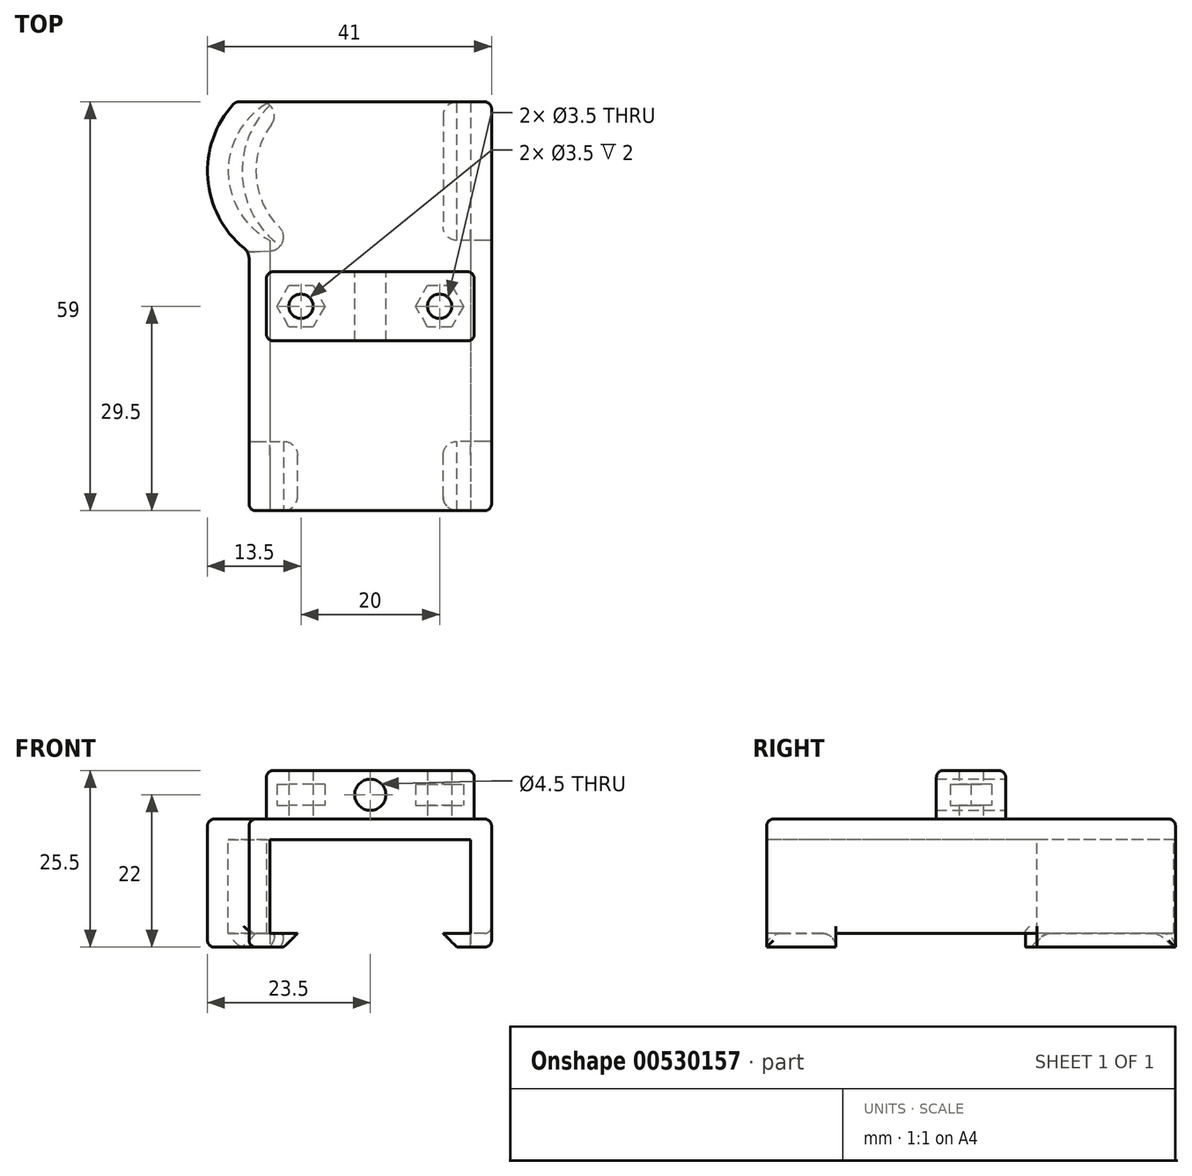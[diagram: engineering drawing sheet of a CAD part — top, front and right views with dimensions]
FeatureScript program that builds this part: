
annotation { "Feature Type Name" : "Feature", "Feature Type Description" : "" }
export const myFeature = defineFeature(function(context is Context, id is Id, definition is map)
    precondition{}
    {
        {
            var Q0;
            Q0=qCreatedBy(makeId("Top.planeOp"),FACE);
            var sketch = newSketch(context, id + "F0", { "sketchPlane" : qUnion([Q0])});
            skLineSegment(sketch, "E0.bottom", {"start": v(-14.5, 29.5) * mm, "end": v(14.5, 29.5) * mm});
            skLineSegment(sketch, "E0.top", {"start": v(-14.5, -29.5) * mm, "end": v(14.5, -29.5) * mm});
            skLineSegment(sketch, "E0.left", {"start": v(-14.5, 9.5) * mm, "end": v(-14.5, -29.5) * mm});
            skLineSegment(sketch, "E0.right", {"start": v(14.5, 29.5) * mm, "end": v(14.5, -29.5) * mm});
            skPoint(sketch, "E0.middle", {"position": v(0, 0) * mm});
            skArc(sketch, "E1", {"start": v(-14.5, 29.5) * mm, "mid": v(-20.5, 19.5) * mm, "end": v(-14.5, 9.5) * mm});
            skLineSegment(sketch, "E2", {"start": v(-29.83, 19.5) * mm, "end": v(45.18, 19.5) * mm, "construction": true});
            skPoint(sketch, "E3", {"position": v(-14.5, 29.5) * mm});
            skPoint(sketch, "E4", {"position": v(-14.5, 9.5) * mm});
            skSolve(sketch);
        }
        {
            var Q0;
            Q0=makeQuery(id+"F0.imprint","IMPRINT",FACE,{"disambiguationData":[TD([[makeQuery(id+"F0.imprint","IMPRINT",EDGE,{"derivedFrom":sQuery(id+"F0.wireOp",EDGE,"E0.bottom")}),-1.0]])]});
            extrude(context, id + "F1", {"entities" : qUnion([Q0]), "oppositeDirection" : true, "depth" : 3 * mm, "offsetDistance" : 25 * mm});
        }
        {
            var Q0;
            Q0=makeQuery(id+"F1.opExtrude","CAP_FACE",FACE,{"disambiguationData":[OSD([sQuery(id+"F0.wireOp",EDGE,"E0.bottom"),sQuery(id+"F0.wireOp",EDGE,"E0.top"),sQuery(id+"F0.wireOp",EDGE,"E0.left"),sQuery(id+"F0.wireOp",EDGE,"E0.right"),sQuery(id+"F0.wireOp",EDGE,"E1")])],"isStart":false});
            var sketch = newSketch(context, id + "F2", { "sketchPlane" : qUnion([Q0])});
            skLineSegment(sketch, "E5.0", {"start": v(14.5, -29.5) * mm, "end": v(14.5, 29.5) * mm});
            skLineSegment(sketch, "E6.0", {"start": v(-14.5, -9.5) * mm, "end": v(-14.5, 29.5) * mm});
            skArc(sketch, "E7.0", {"start": v(-14.5, -29.5) * mm, "mid": v(-20.5, -19.5) * mm, "end": v(-14.5, -9.5) * mm});
            skLineSegment(sketch, "E8.0", {"start": v(17.5, -29.5) * mm, "end": v(17.5, 29.5) * mm});
            skLineSegment(sketch, "E9.0", {"start": v(-17.5, -7.84) * mm, "end": v(-17.5, 29.5) * mm});
            skArc(sketch, "E9.1", {"start": v(-15.91, -32.15) * mm, "mid": v(-23.47, -20.43) * mm, "end": v(-17.5, -7.84) * mm});
            skLineSegment(sketch, "E10", {"start": v(14.5, -29.5) * mm, "end": v(17.5, -29.5) * mm});
            skLineSegment(sketch, "E11", {"start": v(14.5, 29.5) * mm, "end": v(17.5, 29.5) * mm});
            skLineSegment(sketch, "E12", {"start": v(-14.5, 29.5) * mm, "end": v(-17.5, 29.5) * mm});
            skLineSegment(sketch, "E13", {"start": v(-14.5, -29.5) * mm, "end": v(-19.44, -29.5) * mm});
            skSolve(sketch);
        }
        {
            var Q0;
            Q0=makeQuery(id+"F2.imprint","IMPRINT",FACE,{"disambiguationData":[TD([[makeQuery(id+"F2.imprint","IMPRINT",EDGE,{"derivedFrom":sQuery(id+"F2.wireOp",EDGE,"E5.0")}),-1.0]])]});
            var Q1;
            Q1=makeQuery(id+"F2.imprint","IMPRINT",FACE,{"disambiguationData":[TD([[makeQuery(id+"F2.imprint","IMPRINT",EDGE,{"derivedFrom":sQuery(id+"F2.wireOp",EDGE,"E6.0")}),1.0]])]});
            var Q2;
            Q2=makeQuery(id+"F1.opExtrude","CAP_FACE",FACE,{"disambiguationData":[OSD([sQuery(id+"F0.wireOp",EDGE,"E0.bottom"),sQuery(id+"F0.wireOp",EDGE,"E0.top"),sQuery(id+"F0.wireOp",EDGE,"E0.left"),sQuery(id+"F0.wireOp",EDGE,"E0.right"),sQuery(id+"F0.wireOp",EDGE,"E1")])],"isStart":true});
            extrude(context, id + "F3", {"entities" : qUnion([Q0, Q1]), "operationType" : NewBodyOperationType.ADD, "depth" : 13.5 * mm, "offsetDistance" : 25 * mm, "hasSecondDirection" : true, "secondDirectionBound" : BoundingType.UP_TO_SURFACE, "secondDirectionOppositeDirection" : true, "secondDirectionDepth" : 25 * mm, "secondDirectionBoundEntityFace" : qUnion([Q2])});
        }
        {
            var Q0;
            Q0=makeQuery(id+"F3.opExtrude","CAP_FACE",FACE,{"disambiguationData":[OSD([sQuery(id+"F2.wireOp",EDGE,"E6.0"),sQuery(id+"F2.wireOp",EDGE,"E7.0"),sQuery(id+"F2.wireOp",EDGE,"E9.0"),sQuery(id+"F2.wireOp",EDGE,"E9.1"),sQuery(id+"F2.wireOp",EDGE,"E12"),sQuery(id+"F2.wireOp",EDGE,"E13")])],"isStart":false});
            var sketch = newSketch(context, id + "F4", { "sketchPlane" : qUnion([Q0])});
            skLineSegment(sketch, "E14.bottom", {"start": v(-17.5, 29.5) * mm, "end": v(-10.5, 29.5) * mm});
            skLineSegment(sketch, "E14.top", {"start": v(-17.5, 19.5) * mm, "end": v(-10.5, 19.5) * mm});
            skLineSegment(sketch, "E14.left", {"start": v(-17.5, 29.5) * mm, "end": v(-17.5, 19.5) * mm});
            skLineSegment(sketch, "E14.right", {"start": v(-10.5, 29.5) * mm, "end": v(-10.5, 19.5) * mm});
            skLineSegment(sketch, "E15.bottom", {"start": v(17.5, 29.5) * mm, "end": v(10.5, 29.5) * mm});
            skLineSegment(sketch, "E15.top", {"start": v(17.5, 19.5) * mm, "end": v(10.5, 19.5) * mm});
            skLineSegment(sketch, "E15.left", {"start": v(17.5, 29.5) * mm, "end": v(17.5, 19.5) * mm});
            skLineSegment(sketch, "E15.right", {"start": v(10.5, 29.5) * mm, "end": v(10.5, 19.5) * mm});
            skLineSegment(sketch, "E16.bottom", {"start": v(17.5, -29.5) * mm, "end": v(10.5, -29.5) * mm});
            skLineSegment(sketch, "E16.top", {"start": v(17.5, -9.5) * mm, "end": v(10.5, -9.5) * mm});
            skLineSegment(sketch, "E16.left", {"start": v(17.5, -29.5) * mm, "end": v(17.5, -9.5) * mm});
            skLineSegment(sketch, "E16.right", {"start": v(10.5, -29.5) * mm, "end": v(10.5, -9.5) * mm});
            skArc(sketch, "E17.0", {"start": v(-19.44, -29.5) * mm, "mid": v(-23.44, -18.22) * mm, "end": v(-17.5, -7.84) * mm});
            skArc(sketch, "E18", {"start": v(-7.27, -8.36) * mm, "mid": v(-16.37, -17.8) * mm, "end": v(-10.5, -29.5) * mm});
            skLineSegment(sketch, "E19", {"start": v(-19.44, -29.5) * mm, "end": v(-10.5, -29.5) * mm});
            skLineSegment(sketch, "E20", {"start": v(-17.5, -7.84) * mm, "end": v(-7.27, -8.36) * mm});
            skSolve(sketch);
        }
        {
            var Q0;
            Q0 = qSketchRegion(id + "F4", true);
            extrude(context, id + "F5", {"entities" : qUnion([Q0]), "operationType" : NewBodyOperationType.ADD, "depth" : 2 * mm, "offsetDistance" : 25 * mm});
        }
        {
            var Q0;
            Q0=makeQuery(id+"F5.opExtrude","SWEPT_EDGE",EDGE,{"disambiguationData":[OSD([sQuery(id+"F4.wireOp",EDGE,"E18"),sQuery(id+"F4.wireOp",EDGE,"E20")])]});
            var Q1;
            Q1=makeQuery(id+"F5.opExtrude","SWEPT_EDGE",EDGE,{"disambiguationData":[OSD([sQuery(id+"F4.wireOp",EDGE,"E18"),sQuery(id+"F4.wireOp",EDGE,"E19")])]});
            var Q2;
            Q2=makeQuery(id+"F5.opExtrude","SWEPT_EDGE",EDGE,{"disambiguationData":[OSD([sQuery(id+"F4.wireOp",EDGE,"E16.top"),sQuery(id+"F4.wireOp",EDGE,"E16.right")])]});
            var Q3;
            Q3=makeQuery(id+"F5.opExtrude","SWEPT_EDGE",EDGE,{"disambiguationData":[OSD([sQuery(id+"F4.wireOp",EDGE,"E16.bottom"),sQuery(id+"F4.wireOp",EDGE,"E16.right")])]});
            var Q4;
            Q4=makeQuery(id+"F5.opExtrude","SWEPT_EDGE",EDGE,{"disambiguationData":[OSD([sQuery(id+"F4.wireOp",EDGE,"E15.bottom"),sQuery(id+"F4.wireOp",EDGE,"E15.right")])]});
            var Q5;
            Q5=makeQuery(id+"F5.opExtrude","SWEPT_EDGE",EDGE,{"disambiguationData":[OSD([sQuery(id+"F4.wireOp",EDGE,"E15.top"),sQuery(id+"F4.wireOp",EDGE,"E15.right")])]});
            var Q6;
            Q6=makeQuery(id+"F5.opExtrude","SWEPT_EDGE",EDGE,{"disambiguationData":[OSD([sQuery(id+"F4.wireOp",EDGE,"E14.top"),sQuery(id+"F4.wireOp",EDGE,"E14.right")])]});
            var Q7;
            Q7=makeQuery(id+"F5.opExtrude","SWEPT_EDGE",EDGE,{"disambiguationData":[OSD([sQuery(id+"F4.wireOp",EDGE,"E14.bottom"),sQuery(id+"F4.wireOp",EDGE,"E14.right")])]});
            var Q8;
            Q8=makeQuery(id+"F3.opExtrude","SWEPT_EDGE",EDGE,{"disambiguationData":[OSD([sQuery(id+"F2.wireOp",EDGE,"E9.0"),sQuery(id+"F2.wireOp",EDGE,"E9.1")])]});
            var Q9;
            {var subQ0=sQuery(id+"F4.wireOp",EDGE,"E16.top");Q9=makeQuery(id+"F5.boolean.opBoolean","SPLIT",EDGE,{"disambiguationData":[topologyDisambiguationEdgeConnected([makeQuery(id+"F3.opExtrude","CAP_FACE",FACE,{"disambiguationData":[OSD([sQuery(id+"F2.wireOp",EDGE,"E5.0"),sQuery(id+"F2.wireOp",EDGE,"E8.0"),sQuery(id+"F2.wireOp",EDGE,"E10"),sQuery(id+"F2.wireOp",EDGE,"E11")])],"isStart":false})])],"derivedFrom":makeQuery(id+"F5.opExtrude","CAP_EDGE",EDGE,{"disambiguationData":[OSD([subQ0])],"isStart":true})});}
            var Q10;
            {var subQ0=sQuery(id+"F4.wireOp",EDGE,"E14.top");Q10=makeQuery(id+"F5.boolean.opBoolean","SPLIT",EDGE,{"disambiguationData":[topologyDisambiguationEdgeConnected([makeQuery(id+"F3.opExtrude","CAP_FACE",FACE,{"disambiguationData":[OSD([sQuery(id+"F2.wireOp",EDGE,"E6.0"),sQuery(id+"F2.wireOp",EDGE,"E7.0"),sQuery(id+"F2.wireOp",EDGE,"E9.0"),sQuery(id+"F2.wireOp",EDGE,"E9.1"),sQuery(id+"F2.wireOp",EDGE,"E12"),sQuery(id+"F2.wireOp",EDGE,"E13")])],"isStart":false})])],"derivedFrom":makeQuery(id+"F5.opExtrude","CAP_EDGE",EDGE,{"disambiguationData":[OSD([subQ0])],"isStart":true})});}
            var Q11;
            {var subQ0=sQuery(id+"F4.wireOp",EDGE,"E15.top");Q11=makeQuery(id+"F5.boolean.opBoolean","SPLIT",EDGE,{"disambiguationData":[topologyDisambiguationEdgeConnected([makeQuery(id+"F3.opExtrude","CAP_FACE",FACE,{"disambiguationData":[OSD([sQuery(id+"F2.wireOp",EDGE,"E5.0"),sQuery(id+"F2.wireOp",EDGE,"E8.0"),sQuery(id+"F2.wireOp",EDGE,"E10"),sQuery(id+"F2.wireOp",EDGE,"E11")])],"isStart":false})])],"derivedFrom":makeQuery(id+"F5.opExtrude","CAP_EDGE",EDGE,{"disambiguationData":[OSD([subQ0])],"isStart":true})});}
            fillet(context, id + "F6", {"entities" : qUnion([Q0, Q1, Q2, Q3, Q4, Q5, Q6, Q7, Q8, Q9, Q10, Q11]), "tangentPropagation" : true, "radius" : 2 * mm, "defaultsChanged" : false, "vertexSettings" : [], "allowEdgeOverflow" : false});
        }
        {
            var Q0;
            Q0=makeQuery(id+"F5.opExtrude","CAP_EDGE",EDGE,{"disambiguationData":[OSD([sQuery(id+"F4.wireOp",EDGE,"E17.0")])],"isStart":false});
            var Q1;
            Q1=makeQuery(id+"F3.opExtrude","CAP_EDGE",EDGE,{"disambiguationData":[OSD([sQuery(id+"F2.wireOp",EDGE,"E9.0")])],"isStart":false});
            var Q2;
            Q2=makeQuery(id+"F5.opExtrude","CAP_EDGE",EDGE,{"disambiguationData":[OSD([sQuery(id+"F4.wireOp",EDGE,"E14.left")])],"isStart":false});
            var Q3;
            Q3=makeQuery(id+"F3.opExtrude","CAP_EDGE",EDGE,{"disambiguationData":[OSD([sQuery(id+"F2.wireOp",EDGE,"E9.0")])],"isStart":true});
            var Q4;
            Q4=makeQuery(id+"F3.opExtrude","CAP_EDGE",EDGE,{"disambiguationData":[OSD([sQuery(id+"F2.wireOp",EDGE,"E8.0")])],"isStart":false});
            var Q5;
            Q5=makeQuery(id+"F3.opExtrude","CAP_EDGE",EDGE,{"disambiguationData":[OSD([sQuery(id+"F2.wireOp",EDGE,"E8.0")])],"isStart":true});
            var Q6;
            Q6=makeQuery(id+"F3.boolean.opBoolean","MERGE",EDGE,{"derivedFrom":[makeQuery(id+"F1.opExtrude","CAP_EDGE",EDGE,{"disambiguationData":[OSD([sQuery(id+"F0.wireOp",EDGE,"E0.bottom")])],"isStart":true}),makeQuery(id+"F3.opExtrude","CAP_EDGE",EDGE,{"disambiguationData":[OSD([sQuery(id+"F2.wireOp",EDGE,"E10")])],"isStart":true}),makeQuery(id+"F3.opExtrude","CAP_EDGE",EDGE,{"disambiguationData":[OSD([sQuery(id+"F2.wireOp",EDGE,"E13")])],"isStart":true})]});
            var Q7;
            Q7=makeQuery(id+"F3.boolean.opBoolean","MERGE",EDGE,{"derivedFrom":[makeQuery(id+"F1.opExtrude","CAP_EDGE",EDGE,{"disambiguationData":[OSD([sQuery(id+"F0.wireOp",EDGE,"E0.top")])],"isStart":true}),makeQuery(id+"F3.opExtrude","CAP_EDGE",EDGE,{"disambiguationData":[OSD([sQuery(id+"F2.wireOp",EDGE,"E11")])],"isStart":true}),makeQuery(id+"F3.opExtrude","CAP_EDGE",EDGE,{"disambiguationData":[OSD([sQuery(id+"F2.wireOp",EDGE,"E12")])],"isStart":true})]});
            var Q8;
            Q8=makeQuery(id+"F5.boolean.opBoolean","MERGE",EDGE,{"derivedFrom":[makeQuery(id+"F3.opExtrude","SWEPT_EDGE",EDGE,{"disambiguationData":[OSD([sQuery(id+"F2.wireOp",EDGE,"E8.0"),sQuery(id+"F2.wireOp",EDGE,"E11")])]}),makeQuery(id+"F5.opExtrude","SWEPT_EDGE",EDGE,{"disambiguationData":[OSD([sQuery(id+"F4.wireOp",EDGE,"E15.bottom"),sQuery(id+"F4.wireOp",EDGE,"E15.left")])]})]});
            var Q9;
            Q9=makeQuery(id+"F5.boolean.opBoolean","MERGE",EDGE,{"derivedFrom":[makeQuery(id+"F3.opExtrude","SWEPT_EDGE",EDGE,{"disambiguationData":[OSD([sQuery(id+"F2.wireOp",EDGE,"E9.0"),sQuery(id+"F2.wireOp",EDGE,"E12")])]}),makeQuery(id+"F5.opExtrude","SWEPT_EDGE",EDGE,{"disambiguationData":[OSD([sQuery(id+"F4.wireOp",EDGE,"E14.bottom"),sQuery(id+"F4.wireOp",EDGE,"E14.left")])]})]});
            var Q10;
            Q10=makeQuery(id+"F5.boolean.opBoolean","MERGE",EDGE,{"derivedFrom":[makeQuery(id+"F3.opExtrude","SWEPT_EDGE",EDGE,{"disambiguationData":[OSD([sQuery(id+"F2.wireOp",EDGE,"E8.0"),sQuery(id+"F2.wireOp",EDGE,"E10")])]}),makeQuery(id+"F5.opExtrude","SWEPT_EDGE",EDGE,{"disambiguationData":[OSD([sQuery(id+"F4.wireOp",EDGE,"E16.bottom"),sQuery(id+"F4.wireOp",EDGE,"E16.left")])]})]});
            var Q11;
            Q11=makeQuery(id+"F5.boolean.opBoolean","MERGE",EDGE,{"derivedFrom":[makeQuery(id+"F3.opExtrude","SWEPT_EDGE",EDGE,{"disambiguationData":[OSD([sQuery(id+"F2.wireOp",EDGE,"E9.1"),sQuery(id+"F2.wireOp",EDGE,"E13")])]}),makeQuery(id+"F5.opExtrude","SWEPT_EDGE",EDGE,{"disambiguationData":[OSD([sQuery(id+"F4.wireOp",EDGE,"E17.0"),sQuery(id+"F4.wireOp",EDGE,"E19")])]})]});
            var Q12;
            Q12=makeQuery(id+"F5.opExtrude","CAP_EDGE",EDGE,{"disambiguationData":[OSD([sQuery(id+"F4.wireOp",EDGE,"E16.left")])],"isStart":false});
            var Q13;
            Q13=makeQuery(id+"F5.opExtrude","CAP_EDGE",EDGE,{"disambiguationData":[OSD([sQuery(id+"F4.wireOp",EDGE,"E15.left")])],"isStart":false});
            fillet(context, id + "F7", {"entities" : qUnion([Q0, Q1, Q2, Q3, Q4, Q5, Q6, Q7, Q8, Q9, Q10, Q11, Q12, Q13]), "tangentPropagation" : true, "radius" : 1 * mm, "defaultsChanged" : false, "vertexSettings" : [], "allowEdgeOverflow" : false});
        }
        {
            var Q0;
            Q0=makeQuery(id+"F5.opExtrude","CAP_EDGE",EDGE,{"disambiguationData":[OSD([sQuery(id+"F4.wireOp",EDGE,"E16.right")])],"isStart":false});
            var Q1;
            Q1=makeQuery(id+"F5.opExtrude","CAP_EDGE",EDGE,{"disambiguationData":[OSD([sQuery(id+"F4.wireOp",EDGE,"E18")])],"isStart":false});
            var Q2;
            Q2=makeQuery(id+"F5.opExtrude","CAP_EDGE",EDGE,{"disambiguationData":[OSD([sQuery(id+"F4.wireOp",EDGE,"E14.right")])],"isStart":false});
            var Q3;
            Q3=makeQuery(id+"F5.opExtrude","CAP_EDGE",EDGE,{"disambiguationData":[OSD([sQuery(id+"F4.wireOp",EDGE,"E15.right")])],"isStart":false});
            chamfer(context, id + "F8", {"entities" : qUnion([Q0, Q1, Q2, Q3]), "width" : 2 * mm});
        }
        {
            var Q0;
            Q0=makeQuery(id+"F0.imprint","IMPRINT",FACE,{"disambiguationData":[TD([[makeQuery(id+"F0.imprint","IMPRINT",EDGE,{"derivedFrom":sQuery(id+"F0.wireOp",EDGE,"E0.bottom")}),-1.0]])]});
            var sketch = newSketch(context, id + "F9", { "sketchPlane" : qUnion([Q0])});
            skLineSegment(sketch, "E21.bottom", {"start": v(-15, 5) * mm, "end": v(15, 5) * mm});
            skLineSegment(sketch, "E21.top", {"start": v(-15, -5) * mm, "end": v(15, -5) * mm});
            skLineSegment(sketch, "E21.left", {"start": v(-15, 5) * mm, "end": v(-15, -5) * mm});
            skLineSegment(sketch, "E21.right", {"start": v(15, 5) * mm, "end": v(15, -5) * mm});
            skPoint(sketch, "E21.middle", {"position": v(0, 0) * mm});
            skLineSegment(sketch, "E22", {"start": v(-10, 0) * mm, "end": v(0, 0) * mm, "construction": true});
            skLineSegment(sketch, "E23", {"start": v(10, 0) * mm, "end": v(0, 0) * mm, "construction": true});
            skCircle(sketch, "E24.cCircle", {"center": v(-10, 0) * mm, "radius": 3 * mm, "construction": true});
            skLineSegment(sketch, "E24.0", {"start": v(-13.46, 0) * mm, "end": v(-11.73, 3) * mm});
            skLineSegment(sketch, "E24.1", {"start": v(-11.73, 3) * mm, "end": v(-8.27, 3) * mm});
            skLineSegment(sketch, "E24.2", {"start": v(-8.27, 3) * mm, "end": v(-6.54, 0) * mm});
            skLineSegment(sketch, "E24.3", {"start": v(-6.54, 0) * mm, "end": v(-8.27, -3) * mm});
            skLineSegment(sketch, "E24.4", {"start": v(-8.27, -3) * mm, "end": v(-11.73, -3) * mm});
            skLineSegment(sketch, "E24.5", {"start": v(-11.73, -3) * mm, "end": v(-13.46, 0) * mm});
            skPoint(sketch, "E24.0.midPoint", {"position": v(-12.6, 1.5) * mm});
            skCircle(sketch, "E25.cCircle", {"center": v(10, 0) * mm, "radius": 3 * mm, "construction": true});
            skLineSegment(sketch, "E25.0", {"start": v(11.73, 3) * mm, "end": v(13.46, 0) * mm});
            skLineSegment(sketch, "E25.1", {"start": v(13.46, 0) * mm, "end": v(11.73, -3) * mm});
            skLineSegment(sketch, "E25.2", {"start": v(11.73, -3) * mm, "end": v(8.27, -3) * mm});
            skLineSegment(sketch, "E25.3", {"start": v(8.27, -3) * mm, "end": v(6.54, 0) * mm});
            skLineSegment(sketch, "E25.4", {"start": v(6.54, 0) * mm, "end": v(8.27, 3) * mm});
            skLineSegment(sketch, "E25.5", {"start": v(8.27, 3) * mm, "end": v(11.73, 3) * mm});
            skPoint(sketch, "E25.0.midPoint", {"position": v(12.6, 1.5) * mm});
            skCircle(sketch, "E26", {"center": v(-10, 0) * mm, "radius": 1.75 * mm});
            skCircle(sketch, "E27", {"center": v(10, 0) * mm, "radius": 1.75 * mm});
            skSolve(sketch);
        }
        {
            var Q0;
            {var subQ0=sQuery(id+"F9.wireOp",EDGE,"E21.left");Q0=makeQuery(id+"F9.imprint","IMPRINT",FACE,{"disambiguationData":[TD([[makeQuery(id+"F9.imprint","IMPRINT",EDGE,{"derivedFrom":subQ0}),1.0]])]});}
            var Q1;
            Q1=makeQuery(id+"F9.imprint","IMPRINT",FACE,{"disambiguationData":[TD([[makeQuery(id+"F9.imprint","IMPRINT",EDGE,{"derivedFrom":sQuery(id+"F9.wireOp",EDGE,"E24.0")}),1.0]])]});
            var Q2;
            Q2=makeQuery(id+"F9.imprint","IMPRINT",FACE,{"disambiguationData":[TD([[makeQuery(id+"F9.imprint","IMPRINT",EDGE,{"derivedFrom":sQuery(id+"F9.wireOp",EDGE,"E24.0")}),-1.0]])]});
            var Q3;
            {var subQ0=sQuery(id+"F9.wireOp",EDGE,"E21.right");Q3=makeQuery(id+"F9.imprint","IMPRINT",FACE,{"disambiguationData":[TD([[makeQuery(id+"F9.imprint","IMPRINT",EDGE,{"derivedFrom":subQ0}),-1.0]])]});}
            var Q4;
            Q4=makeQuery(id+"F9.imprint","IMPRINT",FACE,{"disambiguationData":[TD([[makeQuery(id+"F9.imprint","IMPRINT",EDGE,{"derivedFrom":sQuery(id+"F9.wireOp",EDGE,"E25.0")}),-1.0]])]});
            extrude(context, id + "F10", {"entities" : qUnion([Q0, Q1, Q2, Q3, Q4]), "operationType" : NewBodyOperationType.ADD, "depth" : 7 * mm, "offsetDistance" : 25 * mm});
        }
        {
            var Q0;
            Q0=makeQuery(id+"F9.imprint","IMPRINT",FACE,{"disambiguationData":[TD([[makeQuery(id+"F9.imprint","IMPRINT",EDGE,{"derivedFrom":sQuery(id+"F9.wireOp",EDGE,"E24.0")}),-1.0]])]});
            var Q1;
            Q1=makeQuery(id+"F9.imprint","IMPRINT",FACE,{"disambiguationData":[TD([[makeQuery(id+"F9.imprint","IMPRINT",EDGE,{"derivedFrom":sQuery(id+"F9.wireOp",EDGE,"E25.0")}),-1.0]])]});
            extrude(context, id + "F11", {"entities" : qUnion([Q0, Q1]), "operationType" : NewBodyOperationType.REMOVE, "depth" : 5 * mm, "offsetDistance" : 25 * mm, "hasSecondDirection" : true, "secondDirectionOppositeDirection" : false, "secondDirectionDepth" : 2 * mm});
        }
        {
            var Q0;
            Q0=makeQuery(id+"F10.opExtrude","SWEPT_FACE",FACE,{"disambiguationData":[OSD([sQuery(id+"F9.wireOp",EDGE,"E21.bottom")])]});
            var sketch = newSketch(context, id + "F12", { "sketchPlane" : qUnion([Q0])});
            skLineSegment(sketch, "E28", {"start": v(-15, 7) * mm, "end": v(15, 0) * mm, "construction": true});
            skCircle(sketch, "E29", {"center": v(0, 3.5) * mm, "radius": 2.25 * mm});
            skSolve(sketch);
        }
        {
            var Q0;
            Q0=makeQuery(id+"F12.imprint","IMPRINT",FACE,{"disambiguationData":[TD([[makeQuery(id+"F12.imprint","IMPRINT",EDGE,{"derivedFrom":sQuery(id+"F12.wireOp",EDGE,"E29")}),1.0]])]});
            extrude(context, id + "F13", {"entities" : qUnion([Q0]), "operationType" : NewBodyOperationType.REMOVE, "endBound" : BoundingType.THROUGH_ALL, "oppositeDirection" : true, "depth" : 25 * mm, "offsetDistance" : 25 * mm});
        }
        {
            var Q0;
            Q0=makeQuery(id+"F1.opExtrude","CAP_EDGE",EDGE,{"disambiguationData":[OSD([sQuery(id+"F0.wireOp",EDGE,"ejjcODVV-JKUh-5dTw-o5So-koxUGDT08wK7")])],"isStart":false});
            var Q1;
            Q1=makeQuery(id+"F10.opExtrude","SWEPT_EDGE",EDGE,{"disambiguationData":[OSD([sQuery(id+"F9.wireOp",EDGE,"E21.bottom"),sQuery(id+"F9.wireOp",EDGE,"E21.left")])]});
            var Q2;
            Q2=makeQuery(id+"F10.opExtrude","SWEPT_EDGE",EDGE,{"disambiguationData":[OSD([sQuery(id+"F9.wireOp",EDGE,"E21.top"),sQuery(id+"F9.wireOp",EDGE,"E21.left")])]});
            var Q3;
            Q3=makeQuery(id+"F10.opExtrude","CAP_EDGE",EDGE,{"disambiguationData":[OSD([sQuery(id+"F9.wireOp",EDGE,"E21.left")])],"isStart":false});
            var Q4;
            Q4=makeQuery(id+"F10.opExtrude","CAP_EDGE",EDGE,{"disambiguationData":[OSD([sQuery(id+"F9.wireOp",EDGE,"E21.bottom")])],"isStart":false});
            var Q5;
            Q5=makeQuery(id+"F10.opExtrude","CAP_EDGE",EDGE,{"disambiguationData":[OSD([sQuery(id+"F9.wireOp",EDGE,"E21.top")])],"isStart":false});
            var Q6;
            Q6=makeQuery(id+"F10.opExtrude","CAP_EDGE",EDGE,{"disambiguationData":[OSD([sQuery(id+"F9.wireOp",EDGE,"E21.right")])],"isStart":false});
            var Q7;
            Q7=makeQuery(id+"F10.opExtrude","SWEPT_EDGE",EDGE,{"disambiguationData":[OSD([sQuery(id+"F9.wireOp",EDGE,"E21.top"),sQuery(id+"F9.wireOp",EDGE,"E21.right")])]});
            var Q8;
            Q8=makeQuery(id+"F10.opExtrude","SWEPT_EDGE",EDGE,{"disambiguationData":[OSD([sQuery(id+"F9.wireOp",EDGE,"E21.bottom"),sQuery(id+"F9.wireOp",EDGE,"E21.right")])]});
            fillet(context, id + "F14", {"entities" : qUnion([Q0, Q1, Q2, Q3, Q4, Q5, Q6, Q7, Q8]), "tangentPropagation" : true, "radius" : 1 * mm, "defaultsChanged" : false, "vertexSettings" : [], "allowEdgeOverflow" : false});
        }
    });
